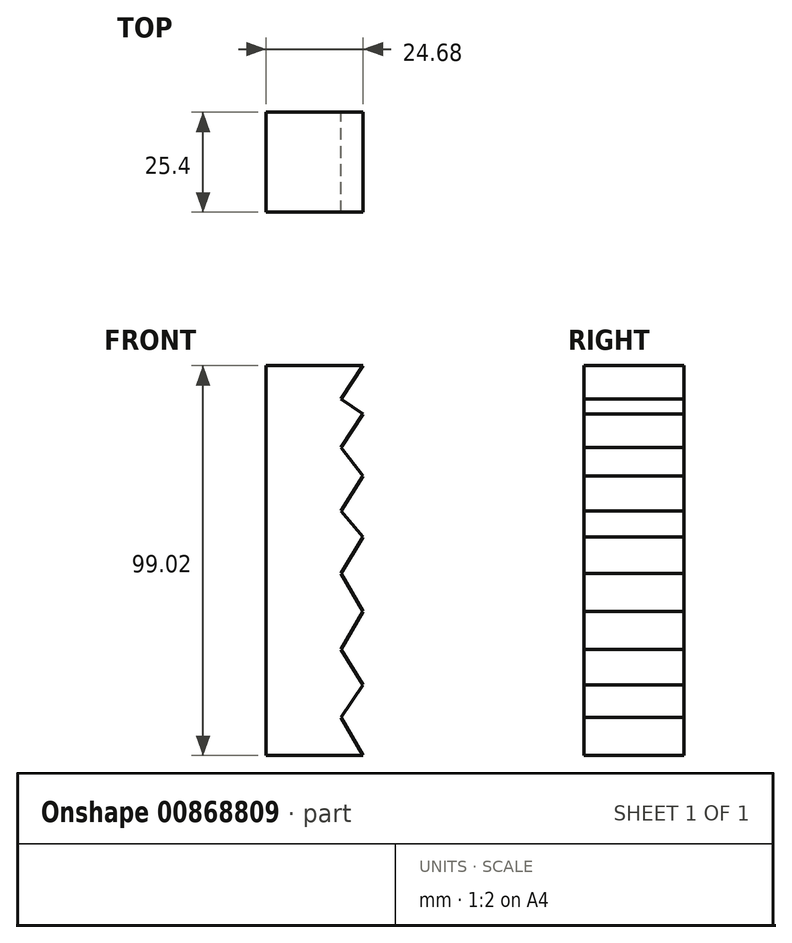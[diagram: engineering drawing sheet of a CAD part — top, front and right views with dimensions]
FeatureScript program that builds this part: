
annotation { "Feature Type Name" : "Feature", "Feature Type Description" : "" }
export const myFeature = defineFeature(function(context is Context, id is Id, definition is map)
    precondition{}
    {
        {
            var Q0;
            Q0=qCreatedBy(makeId("Front.planeOp"),FACE);
            var sketch = newSketch(context, id + "F0", { "sketchPlane" : qUnion([Q0])});
            skLineSegment(sketch, "E0", {"start": v(-38.16, 43.55) * mm, "end": v(-38.16, -55.47) * mm});
            skLineSegment(sketch, "E1", {"start": v(-38.16, -55.47) * mm, "end": v(-13.48, -55.47) * mm});
            skLineSegment(sketch, "E2", {"start": v(-38.16, 43.55) * mm, "end": v(-13.48, 43.55) * mm});
            skLineSegment(sketch, "E3", {"start": v(-13.48, 43.55) * mm, "end": v(-19.15, 35.04) * mm});
            skLineSegment(sketch, "E4", {"start": v(-19.15, 35.04) * mm, "end": v(-13.48, 31.26) * mm});
            skLineSegment(sketch, "E5", {"start": v(-13.48, 31.26) * mm, "end": v(-19.15, 22.75) * mm});
            skLineSegment(sketch, "E6", {"start": v(-19.15, 22.75) * mm, "end": v(-13.48, 15.46) * mm});
            skLineSegment(sketch, "E7", {"start": v(-13.48, 15.46) * mm, "end": v(-19.15, 6.67) * mm});
            skLineSegment(sketch, "E8", {"start": v(-19.15, 6.67) * mm, "end": v(-13.48, 0) * mm});
            skLineSegment(sketch, "E9", {"start": v(-13.48, 0) * mm, "end": v(-19.15, -9.22) * mm});
            skLineSegment(sketch, "E10", {"start": v(-19.15, -9.22) * mm, "end": v(-13.48, -18.87) * mm});
            skLineSegment(sketch, "E11", {"start": v(-13.48, -18.87) * mm, "end": v(-19.15, -28.51) * mm});
            skLineSegment(sketch, "E12", {"start": v(-19.15, -28.51) * mm, "end": v(-13.48, -37.6) * mm});
            skLineSegment(sketch, "E13", {"start": v(-13.48, -37.6) * mm, "end": v(-19.15, -45.82) * mm});
            skLineSegment(sketch, "E14", {"start": v(-19.15, -45.82) * mm, "end": v(-13.48, -55.47) * mm});
            skSolve(sketch);
        }
        {
            var Q0;
            Q0 = qSketchRegion(id + "F0", true);
            extrude(context, id + "F1", {"entities" : qUnion([Q0]), "depth" : 25.4 * mm, "offsetDistance" : 25.4 * mm});
        }
    });
